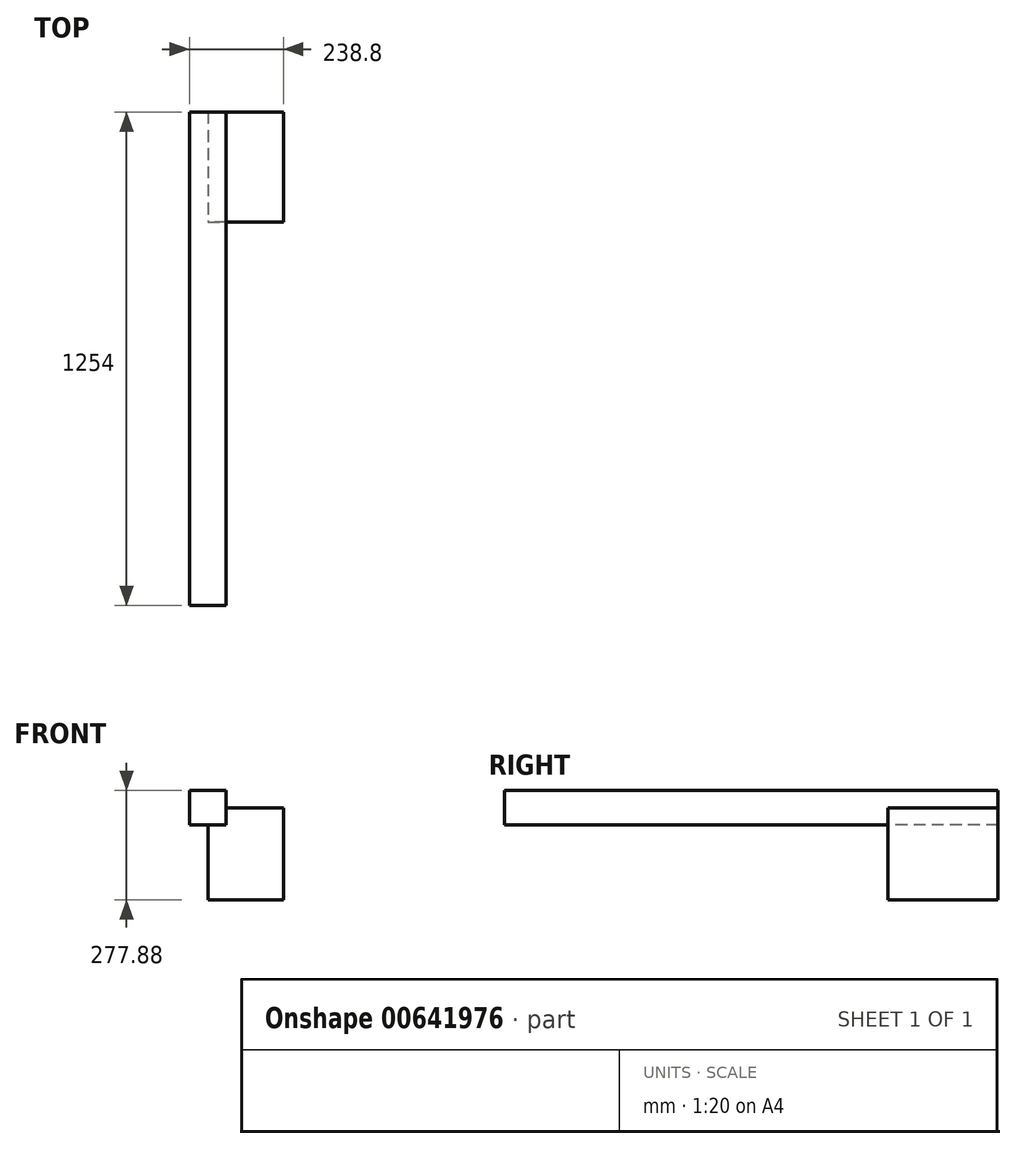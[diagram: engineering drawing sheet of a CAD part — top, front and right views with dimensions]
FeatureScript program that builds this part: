
annotation { "Feature Type Name" : "Feature", "Feature Type Description" : "" }
export const myFeature = defineFeature(function(context is Context, id is Id, definition is map)
    precondition{}
    {
        {
            var Q0;
            Q0=qCreatedBy(makeId("Front.planeOp"),FACE);
            var sketch = newSketch(context, id + "F0", { "sketchPlane" : qUnion([Q0])});
            skLineSegment(sketch, "E0.bottom", {"start": v(46.63, 43.67) * mm, "end": v(-46.63, 43.67) * mm});
            skLineSegment(sketch, "E0.top", {"start": v(46.63, -43.67) * mm, "end": v(-46.63, -43.67) * mm});
            skLineSegment(sketch, "E0.left", {"start": v(46.63, 43.67) * mm, "end": v(46.63, -43.67) * mm});
            skLineSegment(sketch, "E0.right", {"start": v(-46.63, 43.67) * mm, "end": v(-46.63, -43.67) * mm});
            skPoint(sketch, "E0.middle", {"position": v(0, 0) * mm});
            skSolve(sketch);
        }
        {
            var Q0;
            Q0 = qSketchRegion(id + "F0", true);
            extrude(context, id + "F1", {"entities" : qUnion([Q0]), "depth" : 1000 * mm, "offsetDistance" : 25.4 * mm});
        }
        {
            var Q0;
            Q0=qCreatedBy(makeId("Front.planeOp"),FACE);
            var sketch = newSketch(context, id + "F2", { "sketchPlane" : qUnion([Q0])});
            skLineSegment(sketch, "E1.bottom", {"start": v(0, 0) * mm, "end": v(192.17, 0) * mm});
            skLineSegment(sketch, "E1.top", {"start": v(0, -234.21) * mm, "end": v(192.17, -234.21) * mm});
            skLineSegment(sketch, "E1.left", {"start": v(0, 0) * mm, "end": v(0, -234.21) * mm});
            skLineSegment(sketch, "E1.right", {"start": v(192.17, 0) * mm, "end": v(192.17, -234.21) * mm});
            skSolve(sketch);
        }
        {
            var Q0;
            Q0 = qSketchRegion(id + "F2", true);
            extrude(context, id + "F3", {"entities" : qUnion([Q0]), "operationType" : NewBodyOperationType.ADD, "depth" : 25.4 * mm, "offsetDistance" : 25.4 * mm});
        }
        {
            var Q0;
            Q0=makeQuery(id+"F3.boolean.opBoolean","MERGE",FACE,{"derivedFrom":[makeQuery(id+"F1.opExtrude","CAP_FACE",FACE,{"disambiguationData":[OSD([sQuery(id+"F0.wireOp",EDGE,"E0.bottom"),sQuery(id+"F0.wireOp",EDGE,"E0.top"),sQuery(id+"F0.wireOp",EDGE,"E0.left"),sQuery(id+"F0.wireOp",EDGE,"E0.right")])],"isStart":true}),makeQuery(id+"F3.opExtrude","CAP_FACE",FACE,{"disambiguationData":[OSD([sQuery(id+"F2.wireOp",EDGE,"E1.bottom"),sQuery(id+"F2.wireOp",EDGE,"E1.top"),sQuery(id+"F2.wireOp",EDGE,"E1.left"),sQuery(id+"F2.wireOp",EDGE,"E1.right")])],"isStart":true})]});
            extrude(context, id + "F4", {"entities" : qUnion([Q0]), "operationType" : NewBodyOperationType.ADD, "depth" : 254 * mm, "offsetDistance" : 25.4 * mm});
        }
    });
